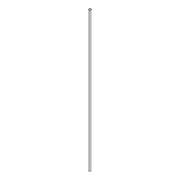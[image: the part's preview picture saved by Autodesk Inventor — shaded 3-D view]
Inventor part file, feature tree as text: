
AUTODESK INVENTOR PART (.ipt)
format: ipt  version: 2022 (Build 260153000, 153)  size: 76,800 bytes
history: native  units: mm
features: extrude x1, sketch x1
ambient origin geometry x8: Origin, YZ Plane, XZ Plane, XY Plane, X Axis, Y Axis, Z Axis, Center Point
bodies: Solid1 (feature_tree)
feature tree (2):
  extrude  "Extrusion1"  Depth=600.0mm
  sketch  "Sketch1"  dims[d0=10.0mm d1=8.0mm d2=600.0mm d3=0.0mm]
